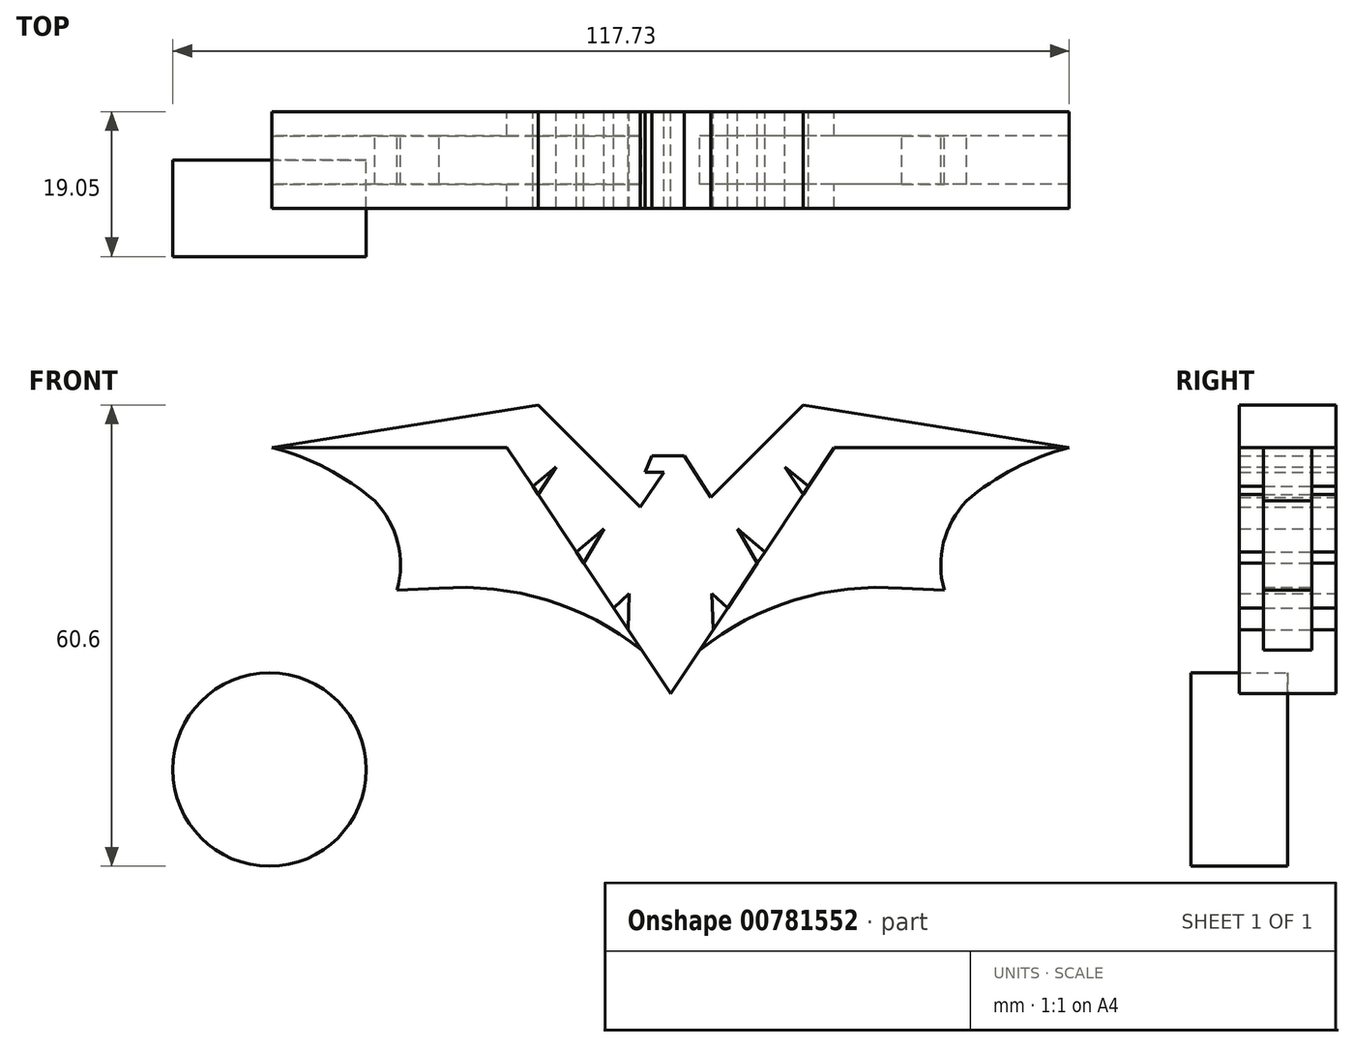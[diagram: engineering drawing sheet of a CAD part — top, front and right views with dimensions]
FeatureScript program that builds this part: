
annotation { "Feature Type Name" : "Feature", "Feature Type Description" : "" }
export const myFeature = defineFeature(function(context is Context, id is Id, definition is map)
    precondition{}
    {
        {
            var Q0;
            Q0=qCreatedBy(makeId("Front.planeOp"),FACE);
            var sketch = newSketch(context, id + "F0", { "sketchPlane" : qUnion([Q0])});
            skLineSegment(sketch, "E0", {"start": v(0, 11.79) * mm, "end": v(-2.46, 11.79) * mm});
            skLineSegment(sketch, "E1", {"start": v(-2.46, 11.79) * mm, "end": v(-3.35, 9.66) * mm});
            skLineSegment(sketch, "E2", {"start": v(-3.35, 9.66) * mm, "end": v(-0.86, 9.66) * mm});
            skLineSegment(sketch, "E3", {"start": v(-0.86, 9.66) * mm, "end": v(-4, 5.12) * mm});
            skLineSegment(sketch, "E4", {"start": v(-4, 5.12) * mm, "end": v(-17.37, 18.49) * mm});
            skLineSegment(sketch, "E5", {"start": v(-17.37, 18.49) * mm, "end": v(-52.35, 12.9) * mm});
            skLineSegment(sketch, "E6", {"start": v(-52.35, 12.9) * mm, "end": v(-21.5, 12.9) * mm});
            skLineSegment(sketch, "E7", {"start": v(-21.5, 12.9) * mm, "end": v(0, -19.45) * mm});
            skLineSegment(sketch, "E8", {"start": v(0, 11.79) * mm, "end": v(1.79, 11.79) * mm});
            skLineSegment(sketch, "E9", {"start": v(1.79, 11.79) * mm, "end": v(5.25, 6.37) * mm});
            skLineSegment(sketch, "E10", {"start": v(5.25, 6.37) * mm, "end": v(17.68, 18.79) * mm});
            skLineSegment(sketch, "E11.MirrorCS", {"start": v(17.37, 18.49) * mm, "end": v(52.35, 12.9) * mm});
            skLineSegment(sketch, "E12.MirrorCS", {"start": v(52.35, 12.9) * mm, "end": v(21.5, 12.9) * mm});
            skLineSegment(sketch, "E13.MirrorCS", {"start": v(21.5, 12.9) * mm, "end": v(0, -19.45) * mm});
            skLineSegment(sketch, "E14", {"start": v(-7.48, -8.2) * mm, "end": v(-5.42, -6.27) * mm});
            skLineSegment(sketch, "E15", {"start": v(-5.42, -6.27) * mm, "end": v(-5.57, -11.07) * mm});
            skLineSegment(sketch, "E16", {"start": v(-12.37, -0.84) * mm, "end": v(-8.77, 2.23) * mm});
            skLineSegment(sketch, "E17", {"start": v(-8.77, 2.23) * mm, "end": v(-11.4, -2.3) * mm});
            skLineSegment(sketch, "E18", {"start": v(-15.02, 10.33) * mm, "end": v(-18.1, 7.79) * mm});
            skLineSegment(sketch, "E19", {"start": v(-15.02, 10.33) * mm, "end": v(-17.4, 6.74) * mm});
            skLineSegment(sketch, "E20.MirrorCS", {"start": v(15.02, 10.33) * mm, "end": v(18.1, 7.79) * mm});
            skLineSegment(sketch, "E21.MirrorCS", {"start": v(15.02, 10.33) * mm, "end": v(17.4, 6.74) * mm});
            skLineSegment(sketch, "E22.MirrorCS", {"start": v(12.37, -0.84) * mm, "end": v(8.77, 2.23) * mm});
            skLineSegment(sketch, "E23.MirrorCS", {"start": v(8.77, 2.23) * mm, "end": v(11.4, -2.3) * mm});
            skLineSegment(sketch, "E24.MirrorCS", {"start": v(7.48, -8.2) * mm, "end": v(5.42, -6.27) * mm});
            skLineSegment(sketch, "E25.MirrorCS", {"start": v(5.42, -6.27) * mm, "end": v(5.57, -11.07) * mm});
            skLineSegment(sketch, "E26", {"start": v(-17.4, 6.74) * mm, "end": v(-18.1, 7.79) * mm});
            skLineSegment(sketch, "E27", {"start": v(-12.37, -0.84) * mm, "end": v(-11.4, -2.3) * mm});
            skLineSegment(sketch, "E28", {"start": v(-7.48, -8.2) * mm, "end": v(-5.57, -11.07) * mm});
            skLineSegment(sketch, "E29", {"start": v(5.57, -11.07) * mm, "end": v(7.48, -8.2) * mm});
            skLineSegment(sketch, "E30", {"start": v(11.4, -2.3) * mm, "end": v(12.37, -0.84) * mm});
            skLineSegment(sketch, "E31", {"start": v(17.4, 6.74) * mm, "end": v(18.1, 7.79) * mm});
            skArc(sketch, "E32", {"start": v(30.38, -5.6) * mm, "mid": v(16.33, -7.12) * mm, "end": v(3.82, -13.7) * mm});
            skLineSegment(sketch, "E33", {"start": v(30.38, -5.6) * mm, "end": v(35.92, -5.82) * mm});
            skArc(sketch, "E34", {"start": v(38.86, 5.9) * mm, "mid": v(35.84, 0.42) * mm, "end": v(35.92, -5.82) * mm});
            skArc(sketch, "E35", {"start": v(52.35, 12.9) * mm, "mid": v(45.2, 10.16) * mm, "end": v(38.86, 5.9) * mm});
            skArc(sketch, "E36.MirrorCS", {"start": v(-30.38, -5.6) * mm, "mid": v(-16.33, -7.12) * mm, "end": v(-3.82, -13.7) * mm});
            skLineSegment(sketch, "E37.MirrorCS", {"start": v(-30.38, -5.6) * mm, "end": v(-35.92, -5.82) * mm});
            skArc(sketch, "E38.MirrorCS", {"start": v(-38.86, 5.9) * mm, "mid": v(-35.84, 0.42) * mm, "end": v(-35.92, -5.82) * mm});
            skArc(sketch, "E39.MirrorCS", {"start": v(-52.35, 12.9) * mm, "mid": v(-45.2, 10.16) * mm, "end": v(-38.86, 5.9) * mm});
            skSolve(sketch);
        }
        {
            var Q0;
            {var subQ15=sQuery(id+"F0.wireOp",EDGE,"ivbOTark-r180-QqLY-gufe-CnPQJXGUDlXY");Q0=makeQuery(id+"F0.imprint","IMPRINT",FACE,{"disambiguationData":[TD([[makeQuery(id+"F0.imprint","IMPRINT",EDGE,{"derivedFrom":subQ15}),-1.0]])]});}
            var Q1;
            Q1=makeQuery(id+"F0.imprint","IMPRINT",FACE,{"disambiguationData":[TD([[makeQuery(id+"F0.imprint","IMPRINT",EDGE,{"derivedFrom":sQuery(id+"F0.wireOp",EDGE,"E0")}),1.0]])]});
            extrude(context, id + "F1", {"entities" : qUnion([Q0, Q1]), "endBound" : BoundingType.SYMMETRIC, "depth" : 12.7 * mm, "offsetDistance" : 25.4 * mm});
        }
        {
            var Q0;
            Q0 = qSketchRegion(id + "F0", true);
            extrude(context, id + "F2", {"entities" : qUnion([Q0]), "operationType" : NewBodyOperationType.ADD, "endBound" : BoundingType.SYMMETRIC, "depth" : 6.35 * mm, "offsetDistance" : 25.4 * mm});
        }
        {
            var Q0;
            Q0=qCreatedBy(makeId("Front.planeOp"),FACE);
            var sketch = newSketch(context, id + "F3", { "sketchPlane" : qUnion([Q0])});
            skCircle(sketch, "E40", {"center": v(-52.68, -29.4) * mm, "radius": 12.7 * mm});
            skSolve(sketch);
        }
        {
            var Q0;
            Q0=makeQuery(id+"F3.imprint","IMPRINT",FACE,{"disambiguationData":[TD([[makeQuery(id+"F3.imprint","IMPRINT",EDGE,{"derivedFrom":sQuery(id+"F3.wireOp",EDGE,"E40")}),1.0]])]});
            extrude(context, id + "F4", {"entities" : qUnion([Q0]), "depth" : 12.7 * mm, "offsetDistance" : 25.4 * mm});
        }
    });
